# Revit family: 306_9e9ca3425b7d4d9db643824018c7ea
name_source: partatom
category: Pipe Accessories
units: mm (PartAtom-declared; Revit-internal decimal feet)

## family parameters
Always vertical = Yes
Cut with Voids When Loaded = No
Part Type = Valve - Breaks Into
Round Connector Dimension = Use Diameter
Shared = No
Work Plane-Based = No

## types (1)
- VTA352 35-60°C G1 -1,5 CV
    A = 32 mm
    A__ve = -32 mm  [stored -0.104987 ft]
    B = 42 mm  [stored 0.137795 ft]
    C = 52 mm  [stored 0.170604 ft]
    CT2 = 21 mm
    D = 25 mm
    DT2 = 13 mm  [stored 0.0426509 ft]
    Description = Thermostatic mixing valve VTA352 CV, PN10 external thread
    L2D = 56 mm
    L2D_Min = 3048 mm  [stored 10 ft]
    LT2 = 28 mm  [stored 0.0918635 ft]
    MC = No
    Manufacturer = ESBE
    QmdConnectorList = 301;D;302;D
    R2 = 11 mm  [stored 0.0360892 ft]
    R3 = 6 mm  [stored 0.019685 ft]
    URL = http://www.esbe.eu
    W1 = 17 mm
    W2D = 25 mm  [stored 0.082021 ft]
    WT2 = 23 mm  [stored 0.0754593 ft]
    X1 = 2 mm  [stored 0.00656168 ft]
    X3 = 52 mm  [stored 0.170604 ft]
    X4 = 48 mm  [stored 0.15748 ft]
    X6 = 7 mm  [stored 0.0229659 ft]
    X7 = 2 mm  [stored 0.00656168 ft]
    Z1 = 14 mm  [stored 0.0459318 ft]
    Z1__ve = -14 mm  [stored -0.0459318 ft]
    Z2 = 5 mm  [stored 0.0164042 ft]
    magiPartTypeId = 306
    magiProductCode = VTA352 35-60°C G1 -1,5 CV
    magiProductFamilyId = 9e9ca3425b7d4d9db643824018c7ea
    magiProductId = b5d0a32bccc8407aae0880c5ec010a

note: [stored X ft] marks values corroborated as IEEE doubles in the binary element streams (Revit-internal decimal feet)

## geometry (parser evidence)
native form markers: Sweep x2
no freeform markers — native parametric forms only
